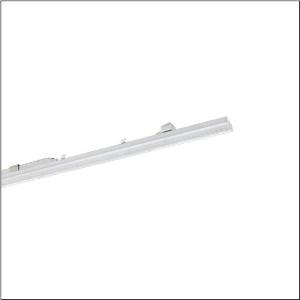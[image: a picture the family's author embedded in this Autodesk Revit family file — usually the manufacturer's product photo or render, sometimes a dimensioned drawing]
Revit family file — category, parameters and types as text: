
# Revit family: tl_l_5wd7a8p0h2b5
name_source: partatom
category: Lighting Fixtures
units: mm (PartAtom-declared; Revit-internal decimal feet)

## family parameters
Cut with Voids When Loaded = No
Host = Face
Light Source = No
Part Type = Normal
Room Calculation Point = No
Round Connector Dimension = Use Diameter
Shared = No

## types (1)
- --- (1 x LED, 5000 lm, 31.5 W, 4000K)
    Apparent Load = 32 VA
    CIE Flux Codes = 49 84 98 100 100
    Color Rendering = 80
    Color Temperature = 4000K
    Default Elevation = 1800 mm
    Description = TL L, luminaire insert, of sheet steel, galvanised, coil coated, white, length: 1.500mm, width: 66mm, height: 67mm, surge protection,LED light colour: 840, control gear: DALI, with terminal, 5-pole, mains connection: 230..240V, AC, 50/60Hz, rated input power: 63W, micro fuse,primary optical cover: cover, of PMMA, light emission: direct distribution, protection rating (complete): as luminaire, insulation class (complete): insulation class I (protective earthing), certification: CE, impact resistance: IK06, permissible ambient temperature for indoor applications: -35..+35°C, standard: NMF01, packaging unit: 1 piece
    Height = 120 mm
    Lamp = 1 x LED
    Lamp Light Flux = 5000 lm
    Lamp Power = 31.5 W
    Lamp count = 1
    Length = 1690 mm
    Luminous efficacy = 159 lm/W
    Manufacturer = Siteco
    ModVariant = No
    Model = 5WD7A8P0H2B5
    Mounting Place = Ceiling
    Mounting Type = Pendant
    Number of Poles = 1
    OnlyDefault = Yes
    Power Factor = 1
    Product Name = TL L
    Product group = luminaire insert
    ProductGroupID = 901
    Protection Class = Protection class I
    Protection Degree = Degree of protection
    RLX_Detail_Level = 1
    RLX_Emergency_Light_Flux = 0 lm
    RLX_Emergency_Type = 0
    RLX_Emergency_Type_DB = No
    RlxData = <blob elided: 17353 chars, md5=bff15d47>
    Socket = socket
    Standby Power = 0 W
    System Light Flux = 5000 lm
    System Power = 32 W
    Type Comments = factory setting: luminous flux: 100 % | dim-lin: 254 | 646 mA
    Type Image = l_1294382.jpg
    URL = http://relux.com
    VarID = @adj_016773
    Voltage = 0 V
    Weight = 0.00 kg
    Width = 208 mm

## geometry (parser evidence)
native form markers: Blend x4, Sweep x11
no freeform markers — native parametric forms only
